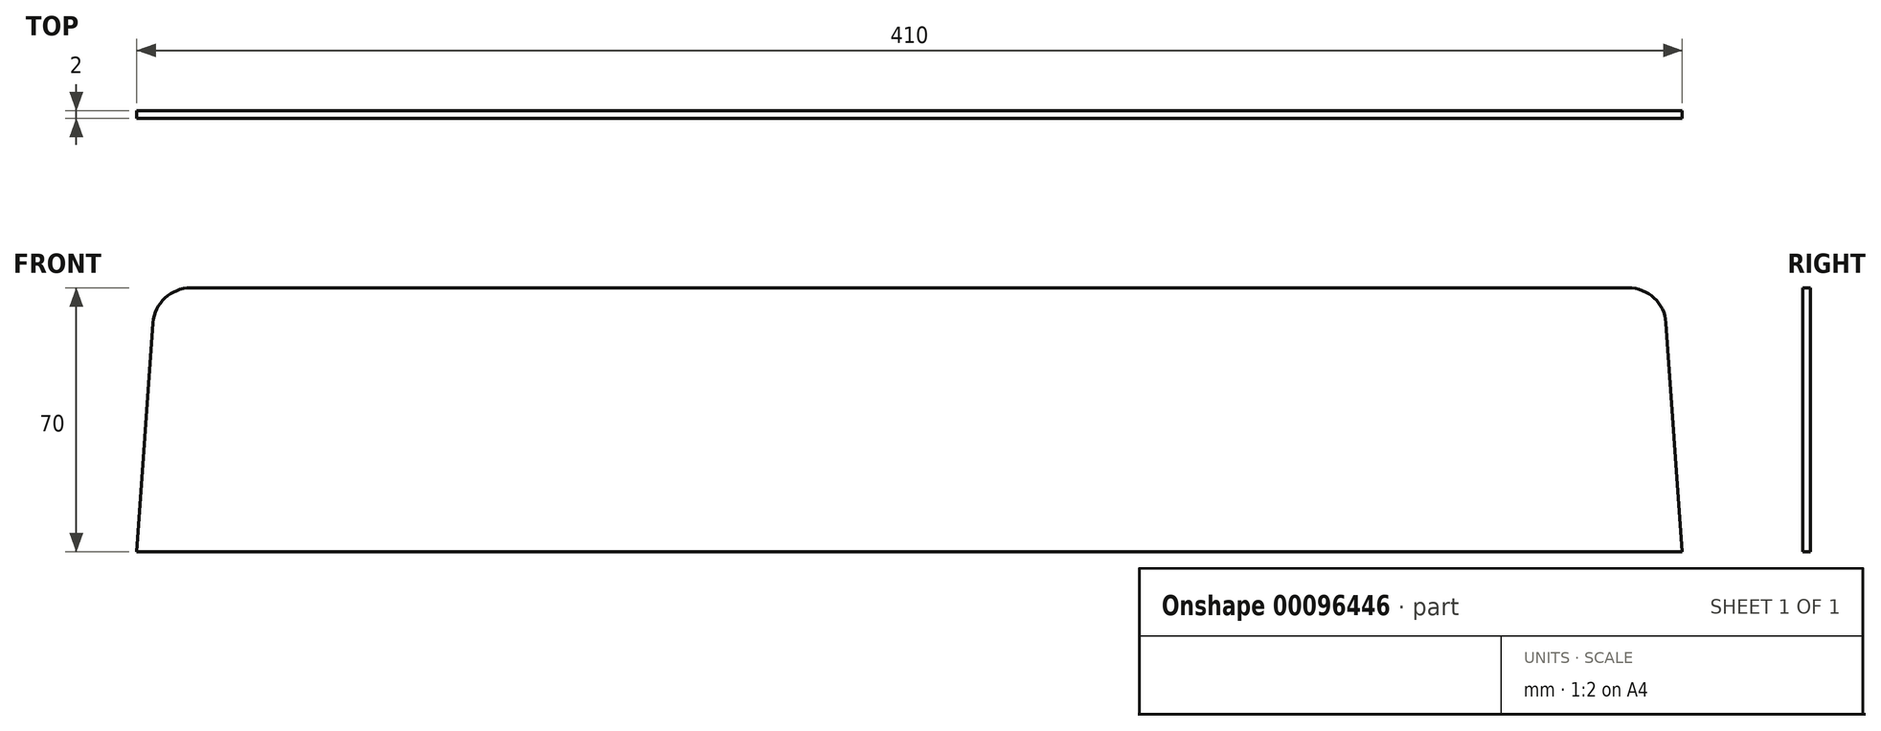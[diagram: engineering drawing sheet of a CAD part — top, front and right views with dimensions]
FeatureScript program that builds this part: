
annotation { "Feature Type Name" : "Feature", "Feature Type Description" : "" }
export const myFeature = defineFeature(function(context is Context, id is Id, definition is map)
    precondition{}
    {
        {
            var Q0;
            Q0=qCreatedBy(makeId("Front.planeOp"),FACE);
            var sketch = newSketch(context, id + "F0", { "sketchPlane" : qUnion([Q0])});
            skLineSegment(sketch, "E0.bottom", {"start": v(0, 0) * mm, "end": v(-205, 0) * mm});
            skLineSegment(sketch, "E0.top", {"start": v(0, 70) * mm, "end": v(-190.69, 70) * mm});
            skLineSegment(sketch, "E0.left", {"start": v(0, 0) * mm, "end": v(0, 70) * mm, "construction": true});
            skLineSegment(sketch, "E0.right", {"start": v(-205, 0) * mm, "end": v(-200.66, 60.71) * mm});
            skPoint(sketch, "E1.visualSharp", {"position": v(-200, 70) * mm});
            skArc(sketch, "E1.filletArc", {"start": v(-190.69, 70) * mm, "mid": v(-197.5, 67.32) * mm, "end": v(-200.66, 60.71) * mm});
            skArc(sketch, "E2.MirrorCS", {"start": v(190.69, 70) * mm, "mid": v(197.5, 67.32) * mm, "end": v(200.66, 60.71) * mm});
            skLineSegment(sketch, "E3.MirrorCS", {"start": v(0, 70) * mm, "end": v(190.69, 70) * mm});
            skLineSegment(sketch, "E4.MirrorCS", {"start": v(0, 0) * mm, "end": v(205, 0) * mm});
            skLineSegment(sketch, "E5.MirrorCS", {"start": v(205, 0) * mm, "end": v(200.66, 60.71) * mm});
            skPoint(sketch, "E6.MirrorP", {"position": v(200, 70) * mm});
            skSolve(sketch);
        }
        {
            var Q0;
            Q0=qSketchRegion(id+"F0",true);
            extrude(context, id + "F1", {"entities" : qUnion([Q0]), "depth" : 2 * mm});
        }
    });
